# Revit family: Franke_Flavor_Station_FS6-A1000_FM_CM(JP)
name_source: partatom
category: Specialty Equipment
revit_build: Autodesk Revit 2015 (Build: 20140606_1530(x64)
units: mm (PartAtom-declared; Revit-internal decimal feet)

## types (2) — shared parameters
Assembly Code = key module Flavor Station
Capacity = up to 6 bottles
Cycle = 50 Hz
Cycle Alternative = 60 Hz
Depth (mm) = 452 mm  [stored 1.48294 ft]
Description = key module Flavor Station enables the automated and constant dosing of syrup in the coffee / milk
Energy loss acc. to DIN 18873 = -
Height (mm) = 544 mm
Keynote = key module Flavor Station
Manufacturer = Franke
Max Overcurrent Protection = -
Model = Flavor Station FS6 - A1000 FM CM
Number of Nutral Conductors = 1
Number of Poles = 1
Number of Protective Conductors = 1
URL = https://www.franke.com
Volts max. = 0 V
Volts min. = 100 V
Watts max. = 0 W
Watts min. = 0 W
Weight = 17 kg
Width (mm) = 200 mm  [stored 0.656168 ft]
zero-valued in all types: Cost

## per-type parameters (varying)
| type | Frontcover |
| Flavor Station FS6 - A1000 FM CM(100V/black line/JP) | Franke Black |
| Flavor Station FS6 - A1000 FM CM(100V/anthracite/JP) | Franke Anthracite |

note: [stored X ft] marks values corroborated as IEEE doubles in the binary element streams (Revit-internal decimal feet)
